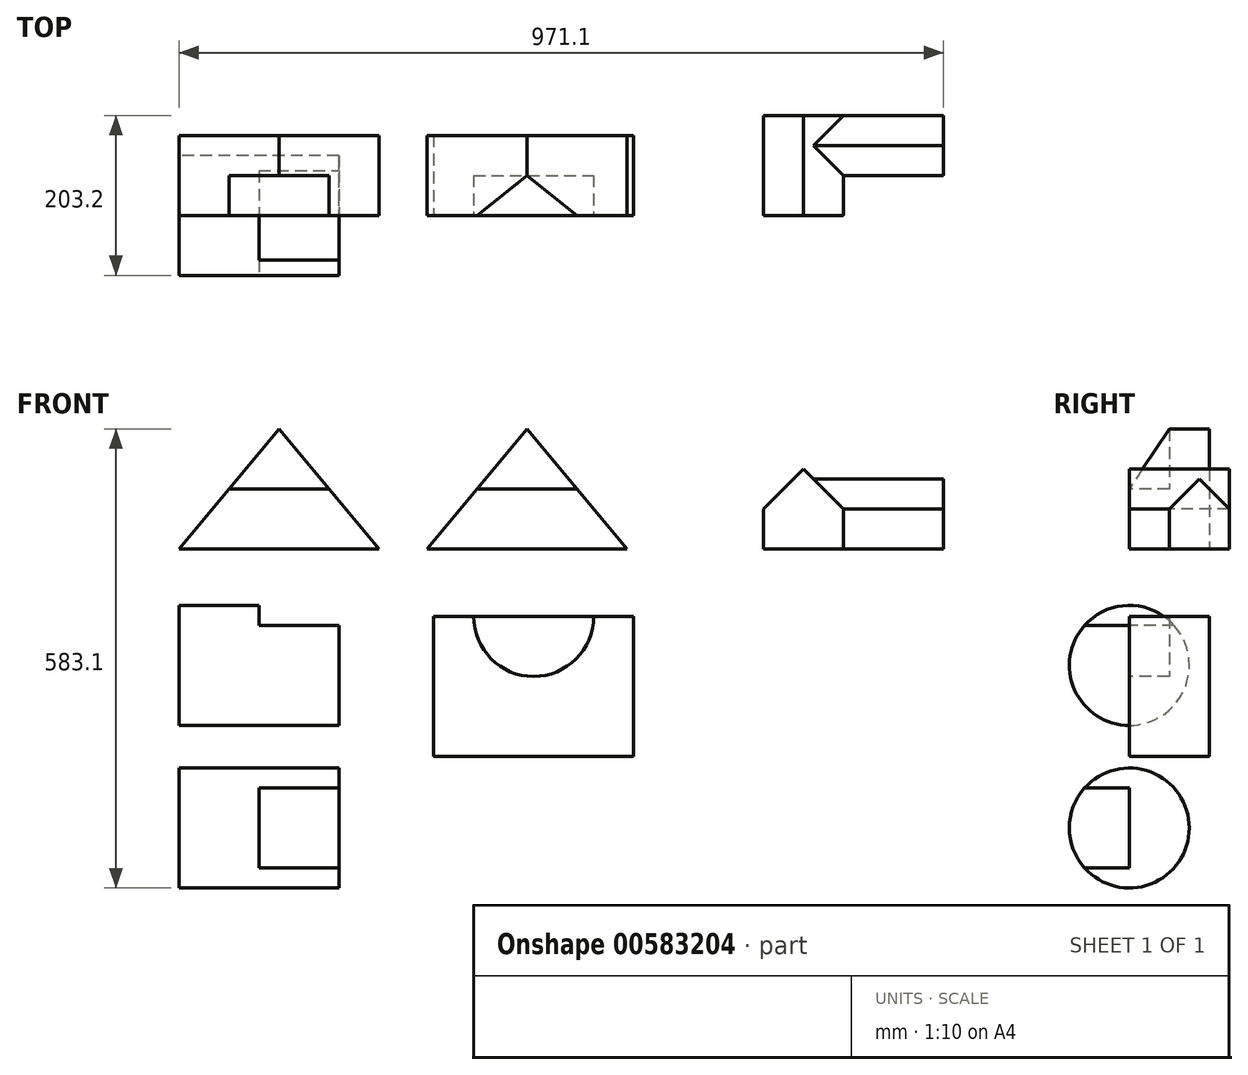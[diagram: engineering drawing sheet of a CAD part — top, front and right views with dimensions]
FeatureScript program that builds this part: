
annotation { "Feature Type Name" : "Feature", "Feature Type Description" : "" }
export const myFeature = defineFeature(function(context is Context, id is Id, definition is map)
    precondition{}
    {
        {
            var Q0;
            Q0=qCreatedBy(makeId("Front.planeOp"),FACE);
            var sketch = newSketch(context, id + "F0", { "sketchPlane" : qUnion([Q0])});
            skLineSegment(sketch, "E0", {"start": v(0, 0) * mm, "end": v(254, 0) * mm});
            skLineSegment(sketch, "E1", {"start": v(127, 152.4) * mm, "end": v(0, 0) * mm});
            skLineSegment(sketch, "E2", {"start": v(127, 152.4) * mm, "end": v(254, 0) * mm});
            skSolve(sketch);
        }
        {
            var Q0;
            Q0=makeQuery(id+"F0.imprint","IMPRINT",FACE,{"disambiguationData":[TD([[makeQuery(id+"F0.imprint","IMPRINT",EDGE,{"derivedFrom":sQuery(id+"F0.wireOp",EDGE,"E0")}),1.0]])]});
            extrude(context, id + "F1", {"entities" : qUnion([Q0]), "oppositeDirection" : true, "depth" : 101.6 * mm, "offsetDistance" : 25.4 * mm});
        }
        {
            var Q0;
            Q0=makeQuery(id+"F1.opExtrude","CAP_FACE",FACE,{"disambiguationData":[OSD([sQuery(id+"F0.wireOp",EDGE,"E0"),sQuery(id+"F0.wireOp",EDGE,"E1"),sQuery(id+"F0.wireOp",EDGE,"E2")])],"isStart":true});
            var sketch = newSketch(context, id + "F2", { "sketchPlane" : qUnion([Q0])});
            skLineSegment(sketch, "E3", {"start": v(127, 76.2) * mm, "end": v(63.5, 76.2) * mm});
            skLineSegment(sketch, "E4", {"start": v(127, 76.2) * mm, "end": v(190.5, 76.2) * mm});
            skLineSegment(sketch, "E5", {"start": v(63.5, 76.2) * mm, "end": v(127, 152.4) * mm});
            skLineSegment(sketch, "E6", {"start": v(127, 152.4) * mm, "end": v(190.5, 76.2) * mm});
            skSolve(sketch);
        }
        {
            var Q0;
            Q0 = qSketchRegion(id + "F2", true);
            extrude(context, id + "F3", {"entities" : qUnion([Q0]), "operationType" : NewBodyOperationType.REMOVE, "oppositeDirection" : true, "depth" : 50.8 * mm, "offsetDistance" : 25.4 * mm});
        }
        {
            var Q0;
            Q0=qCreatedBy(makeId("Front.planeOp"),FACE);
            var sketch = newSketch(context, id + "F4", { "sketchPlane" : qUnion([Q0])});
            skLineSegment(sketch, "E7", {"start": v(315.2, 0) * mm, "end": v(569.2, 0) * mm});
            skLineSegment(sketch, "E8", {"start": v(442.2, 152.4) * mm, "end": v(315.2, 0) * mm});
            skLineSegment(sketch, "E9", {"start": v(442.2, 152.4) * mm, "end": v(569.2, 0) * mm});
            skSolve(sketch);
        }
        {
            var Q0;
            Q0=makeQuery(id+"F4.imprint","IMPRINT",FACE,{"disambiguationData":[TD([[makeQuery(id+"F4.imprint","IMPRINT",EDGE,{"derivedFrom":sQuery(id+"F4.wireOp",EDGE,"E7")}),1.0]])]});
            extrude(context, id + "F5", {"entities" : qUnion([Q0]), "oppositeDirection" : true, "depth" : 101.6 * mm, "offsetDistance" : 25.4 * mm});
        }
        {
            var Q0;
            Q0=makeQuery(id+"F5.opExtrude","CAP_EDGE",EDGE,{"disambiguationData":[OSD([sQuery(id+"F4.wireOp",EDGE,"E7")])],"isStart":true});
            cPoint(context, id + "F6", {"entities" : qUnion([Q0]), "parameter" : 0.5});
        }
        {
            var Q0;
            Q0=makeQuery(id+"F5.opExtrude","CAP_VERTEX",VERTEX,{"disambiguationData":[OSD([sQuery(id+"F4.wireOp",EDGE,"E8"),sQuery(id+"F4.wireOp",EDGE,"E9")])],"isStart":true});
            var Q1;
            Q1=makeQuery(id+"F5.opExtrude","CAP_VERTEX",VERTEX,{"disambiguationData":[OSD([sQuery(id+"F4.wireOp",EDGE,"E8"),sQuery(id+"F4.wireOp",EDGE,"E9")])],"isStart":false});
            var Q2;
            Q2 = qCreatedBy(id + "F6" ,VERTEX);
            cPlane(context, id + "F7", {"entities" : qUnion([Q0, Q1, Q2]), "cplaneType" : CPlaneType.THREE_POINT, "offset" : 127 * mm, "oppositeDirection" : true, "width" : 152.4 * mm, "height" : 152.4 * mm});
        }
        {
            var Q0;
            Q0=qCreatedBy(id+"F7.planeOp",FACE);
            var sketch = newSketch(context, id + "F8", { "sketchPlane" : qUnion([Q0])});
            skLineSegment(sketch, "E10", {"start": v(0, 152.4) * mm, "end": v(50.8, 152.4) * mm});
            skLineSegment(sketch, "E11", {"start": v(0, 152.4) * mm, "end": v(0, 76.2) * mm});
            skLineSegment(sketch, "E12", {"start": v(0, 76.2) * mm, "end": v(50.8, 152.4) * mm});
            skSolve(sketch);
        }
        {
            var Q0;
            Q0 = qSketchRegion(id + "F8", true);
            extrude(context, id + "F9", {"entities" : qUnion([Q0]), "operationType" : NewBodyOperationType.REMOVE, "endBound" : BoundingType.SYMMETRIC, "oppositeDirection" : true, "depth" : 141.22 * mm, "offsetDistance" : 25.4 * mm});
        }
        {
            var Q0;
            Q0=qCreatedBy(makeId("Front.planeOp"),FACE);
            var sketch = newSketch(context, id + "F10", { "sketchPlane" : qUnion([Q0])});
            skLineSegment(sketch, "E13.bottom", {"start": v(742.5, 0) * mm, "end": v(971.1, 0) * mm});
            skLineSegment(sketch, "E13.top", {"start": v(742.5, 101.6) * mm, "end": v(971.1, 101.6) * mm});
            skLineSegment(sketch, "E13.left", {"start": v(742.5, 0) * mm, "end": v(742.5, 101.6) * mm});
            skLineSegment(sketch, "E13.right", {"start": v(971.1, 0) * mm, "end": v(971.1, 101.6) * mm});
            skSolve(sketch);
        }
        {
            var Q0;
            Q0=makeQuery(id+"F10.imprint","IMPRINT",FACE,{"disambiguationData":[TD([[makeQuery(id+"F10.imprint","IMPRINT",EDGE,{"derivedFrom":sQuery(id+"F10.wireOp",EDGE,"E13.bottom")}),1.0]])]});
            extrude(context, id + "F11", {"entities" : qUnion([Q0]), "oppositeDirection" : true, "depth" : 127 * mm, "offsetDistance" : 25.4 * mm});
        }
        {
            var Q0;
            Q0=makeQuery(id+"F11.opExtrude","CAP_FACE",FACE,{"disambiguationData":[OSD([sQuery(id+"F10.wireOp",EDGE,"E13.bottom"),sQuery(id+"F10.wireOp",EDGE,"E13.top"),sQuery(id+"F10.wireOp",EDGE,"E13.left"),sQuery(id+"F10.wireOp",EDGE,"E13.right")])],"isStart":true});
            var sketch = newSketch(context, id + "F12", { "sketchPlane" : qUnion([Q0])});
            skLineSegment(sketch, "E14", {"start": v(742.5, 101.6) * mm, "end": v(793.3, 101.6) * mm});
            skLineSegment(sketch, "E15", {"start": v(742.5, 101.6) * mm, "end": v(742.5, 50.8) * mm});
            skLineSegment(sketch, "E16", {"start": v(793.3, 101.6) * mm, "end": v(742.5, 50.8) * mm});
            skLineSegment(sketch, "E17", {"start": v(793.3, 101.6) * mm, "end": v(844.1, 101.6) * mm});
            skLineSegment(sketch, "E18", {"start": v(844.1, 101.6) * mm, "end": v(844.1, 50.8) * mm});
            skLineSegment(sketch, "E19", {"start": v(844.1, 50.8) * mm, "end": v(793.3, 101.6) * mm});
            skSolve(sketch);
        }
        {
            var Q0;
            Q0 = qSketchRegion(id + "F12", true);
            extrude(context, id + "F13", {"entities" : qUnion([Q0]), "operationType" : NewBodyOperationType.REMOVE, "oppositeDirection" : true, "depth" : 139.7 * mm, "offsetDistance" : 25.4 * mm});
        }
        {
            var Q0;
            Q0=makeQuery(id+"F11.opExtrude","CAP_FACE",FACE,{"disambiguationData":[OSD([sQuery(id+"F10.wireOp",EDGE,"E13.bottom"),sQuery(id+"F10.wireOp",EDGE,"E13.top"),sQuery(id+"F10.wireOp",EDGE,"E13.left"),sQuery(id+"F10.wireOp",EDGE,"E13.right")])],"isStart":true});
            var sketch = newSketch(context, id + "F14", { "sketchPlane" : qUnion([Q0])});
            skPoint(sketch, "E20.endSnap0", {"position": v(971.1, 50.8) * mm});
            skLineSegment(sketch, "E21", {"start": v(844.1, 50.8) * mm, "end": v(844.1, 0) * mm});
            skLineSegment(sketch, "E22.bottom", {"start": v(844.1, 0) * mm, "end": v(971.1, 0) * mm});
            skLineSegment(sketch, "E22.left", {"start": v(844.1, 0) * mm, "end": v(844.1, 50.8) * mm});
            skLineSegment(sketch, "E22.right", {"start": v(971.1, 0) * mm, "end": v(971.1, 50.8) * mm});
            skLineSegment(sketch, "E23", {"start": v(844.1, 50.8) * mm, "end": v(844.1, 101.6) * mm});
            skLineSegment(sketch, "E24", {"start": v(844.1, 101.6) * mm, "end": v(971.1, 101.6) * mm});
            skLineSegment(sketch, "E25", {"start": v(971.1, 101.6) * mm, "end": v(971.1, 50.8) * mm});
            skSolve(sketch);
        }
        {
            var Q0;
            Q0=makeQuery(id+"F11.opExtrude","SWEPT_FACE",FACE,{"disambiguationData":[OSD([sQuery(id+"F10.wireOp",EDGE,"E13.right")])]});
            var sketch = newSketch(context, id + "F15", { "sketchPlane" : qUnion([Q0])});
            skLineSegment(sketch, "E26", {"start": v(50.8, 50.8) * mm, "end": v(88.9, 88.9) * mm});
            skLineSegment(sketch, "E27", {"start": v(88.9, 88.9) * mm, "end": v(127, 50.8) * mm});
            skLineSegment(sketch, "E28", {"start": v(127, 50.8) * mm, "end": v(127, 0) * mm});
            skLineSegment(sketch, "E29", {"start": v(127, 0) * mm, "end": v(50.8, 0) * mm});
            skLineSegment(sketch, "E30", {"start": v(50.8, 0) * mm, "end": v(50.8, 50.8) * mm});
            skSolve(sketch);
        }
        {
            var Q0;
            Q0=makeQuery(id+"F15.imprint","IMPRINT",FACE,{"disambiguationData":[TD([[makeQuery(id+"F15.imprint","IMPRINT",EDGE,{"derivedFrom":sQuery(id+"F15.wireOp",EDGE,"E26")}),-1.0]])]});
            var sketch = newSketch(context, id + "F16", { "sketchPlane" : qUnion([Q0])});
            skLineSegment(sketch, "E31", {"start": v(50.8, 50.8) * mm, "end": v(50.8, 101.6) * mm});
            skLineSegment(sketch, "E32", {"start": v(50.8, 101.6) * mm, "end": v(127, 101.6) * mm});
            skLineSegment(sketch, "E33", {"start": v(127, 101.6) * mm, "end": v(127, 50.8) * mm});
            skLineSegment(sketch, "E34", {"start": v(50.8, 50.8) * mm, "end": v(88.9, 88.9) * mm});
            skLineSegment(sketch, "E35", {"start": v(88.9, 88.9) * mm, "end": v(127, 50.8) * mm});
            skSolve(sketch);
        }
        {
            var Q0;
            Q0 = qSketchRegion(id + "F14", true);
            extrude(context, id + "F17", {"entities" : qUnion([Q0]), "operationType" : NewBodyOperationType.REMOVE, "oppositeDirection" : true, "depth" : 50.8 * mm, "offsetDistance" : 25.4 * mm});
        }
        {
            var Q0;
            Q0=makeQuery(id+"F15.imprint","IMPRINT",FACE,{"disambiguationData":[TD([[makeQuery(id+"F15.imprint","IMPRINT",EDGE,{"derivedFrom":sQuery(id+"F15.wireOp",EDGE,"E26")}),1.0]])]});
            extrude(context, id + "F18", {"entities" : qUnion([Q0]), "operationType" : NewBodyOperationType.REMOVE, "oppositeDirection" : true, "depth" : 127 * mm, "offsetDistance" : 25.4 * mm});
        }
        {
            var Q0;
            Q0=makeQuery(id+"F16.imprint","IMPRINT",FACE,{"disambiguationData":[TD([[makeQuery(id+"F16.imprint","IMPRINT",EDGE,{"derivedFrom":sQuery(id+"F16.wireOp",EDGE,"E34")}),-1.0]])]});
            extrude(context, id + "F19", {"entities" : qUnion([Q0]), "operationType" : NewBodyOperationType.ADD, "oppositeDirection" : true, "depth" : 177.8 * mm, "offsetDistance" : 25.4 * mm});
        }
        {
            var Q0;
            Q0=qCreatedBy(makeId("Right.planeOp"),FACE);
            var sketch = newSketch(context, id + "F20", { "sketchPlane" : qUnion([Q0])});
            skCircle(sketch, "E36", {"center": v(0, -147.9) * mm, "radius": 76.2 * mm});
            skSolve(sketch);
        }
        {
            var Q0;
            Q0=makeQuery(id+"F20.imprint","IMPRINT",FACE,{"disambiguationData":[TD([[makeQuery(id+"F20.imprint","IMPRINT",EDGE,{"derivedFrom":sQuery(id+"F20.wireOp",EDGE,"E36")}),1.0]])]});
            extrude(context, id + "F21", {"entities" : qUnion([Q0]), "depth" : 203.2 * mm, "offsetDistance" : 25.4 * mm});
        }
        {
            var Q0;
            Q0=makeQuery(id+"F21.opExtrude","CAP_FACE",FACE,{"disambiguationData":[OSD([sQuery(id+"F20.wireOp",EDGE,"E36")])],"isStart":false});
            var sketch = newSketch(context, id + "F22", { "sketchPlane" : qUnion([Q0])});
            skLineSegment(sketch, "E37", {"start": v(0, -97.1) * mm, "end": v(-56.8, -97.1) * mm});
            skLineSegment(sketch, "E38", {"start": v(0, -97.1) * mm, "end": v(56.8, -97.1) * mm});
            skSolve(sketch);
        }
        {
            var Q0;
            {var subQ0=sQuery(id+"F22.wireOp",EDGE,"E37");Q0=makeQuery(id+"F22.imprint","IMPRINT",FACE,{"disambiguationData":[TD([[makeQuery(id+"F22.imprint","IMPRINT",EDGE,{"derivedFrom":subQ0}),-1.0]])]});}
            extrude(context, id + "F23", {"entities" : qUnion([Q0]), "operationType" : NewBodyOperationType.REMOVE, "oppositeDirection" : true, "depth" : 101.6 * mm, "offsetDistance" : 25.4 * mm});
        }
        {
            var Q0;
            Q0=qCreatedBy(makeId("Right.planeOp"),FACE);
            var sketch = newSketch(context, id + "F24", { "sketchPlane" : qUnion([Q0])});
            skCircle(sketch, "E39", {"center": v(0, -354.5) * mm, "radius": 76.2 * mm});
            skSolve(sketch);
        }
        {
            var Q0;
            Q0=makeQuery(id+"F24.imprint","IMPRINT",FACE,{"disambiguationData":[TD([[makeQuery(id+"F24.imprint","IMPRINT",EDGE,{"derivedFrom":sQuery(id+"F24.wireOp",EDGE,"E39")}),1.0]])]});
            extrude(context, id + "F25", {"entities" : qUnion([Q0]), "depth" : 203.2 * mm, "offsetDistance" : 25.4 * mm});
        }
        {
            var Q0;
            Q0=makeQuery(id+"F25.opExtrude","CAP_FACE",FACE,{"disambiguationData":[OSD([sQuery(id+"F24.wireOp",EDGE,"E39")])],"isStart":false});
            var sketch = newSketch(context, id + "F26", { "sketchPlane" : qUnion([Q0])});
            skLineSegment(sketch, "E40", {"start": v(0, -354.5) * mm, "end": v(0, -303.7) * mm});
            skLineSegment(sketch, "E41", {"start": v(0, -354.5) * mm, "end": v(0, -405.3) * mm});
            skLineSegment(sketch, "E42", {"start": v(0, -303.7) * mm, "end": v(-56.8, -303.7) * mm});
            skLineSegment(sketch, "E43", {"start": v(0, -405.3) * mm, "end": v(-56.8, -405.3) * mm});
            skSolve(sketch);
        }
        {
            var Q0;
            Q0=makeQuery(id+"F26.imprint","IMPRINT",FACE,{"disambiguationData":[TD([[makeQuery(id+"F26.imprint","IMPRINT",EDGE,{"derivedFrom":sQuery(id+"F26.wireOp",EDGE,"E40")}),1.0]])]});
            extrude(context, id + "F27", {"entities" : qUnion([Q0]), "operationType" : NewBodyOperationType.REMOVE, "oppositeDirection" : true, "depth" : 101.6 * mm, "offsetDistance" : 25.4 * mm});
        }
        {
            var Q0;
            Q0=qCreatedBy(makeId("Front.planeOp"),FACE);
            var sketch = newSketch(context, id + "F28", { "sketchPlane" : qUnion([Q0])});
            skLineSegment(sketch, "E44.bottom", {"start": v(323.57, -263.53) * mm, "end": v(577.57, -263.53) * mm});
            skLineSegment(sketch, "E44.top", {"start": v(323.57, -85.73) * mm, "end": v(577.57, -85.73) * mm});
            skLineSegment(sketch, "E44.left", {"start": v(323.57, -263.53) * mm, "end": v(323.57, -85.73) * mm});
            skLineSegment(sketch, "E44.right", {"start": v(577.57, -263.53) * mm, "end": v(577.57, -85.73) * mm});
            skSolve(sketch);
        }
        {
            var Q0;
            Q0=makeQuery(id+"F28.imprint","IMPRINT",FACE,{"disambiguationData":[TD([[makeQuery(id+"F28.imprint","IMPRINT",EDGE,{"derivedFrom":sQuery(id+"F28.wireOp",EDGE,"E44.bottom")}),1.0]])]});
            extrude(context, id + "F29", {"entities" : qUnion([Q0]), "oppositeDirection" : true, "depth" : 101.6 * mm, "offsetDistance" : 25.4 * mm});
        }
        {
            var Q0;
            Q0=makeQuery(id+"F29.opExtrude","CAP_FACE",FACE,{"disambiguationData":[OSD([sQuery(id+"F28.wireOp",EDGE,"E44.bottom"),sQuery(id+"F28.wireOp",EDGE,"E44.top"),sQuery(id+"F28.wireOp",EDGE,"E44.left"),sQuery(id+"F28.wireOp",EDGE,"E44.right")])],"isStart":true});
            var sketch = newSketch(context, id + "F30", { "sketchPlane" : qUnion([Q0])});
            skCircle(sketch, "E45", {"center": v(450.57, -85.73) * mm, "radius": 76.2 * mm});
            skSolve(sketch);
        }
        {
            var Q0;
            {var subQ0=sQuery(id+"F30.wireOp",EDGE,"E45");var subQ1=makeQuery(id+"F29.opExtrude","CAP_EDGE",EDGE,{"disambiguationData":[OSD([sQuery(id+"F28.wireOp",EDGE,"E44.top")])],"isStart":true});var subQ2=makeQuery(id+"F30.imprint","INTERSECT",VERTEX,{"disambiguationData":[OD(0.0)],"derivedFrom":[subQ1,subQ0]});Q0=makeQuery(id+"F30.imprint","IMPRINT",FACE,{"disambiguationData":[TD([[makeQuery(id+"F30.imprint","IMPRINT",EDGE,{"disambiguationData":[TD([[subQ2,-1.0]])],"derivedFrom":subQ0}),1.0]])]});}
            extrude(context, id + "F31", {"entities" : qUnion([Q0]), "operationType" : NewBodyOperationType.REMOVE, "oppositeDirection" : true, "depth" : 50.8 * mm, "offsetDistance" : 25.4 * mm});
        }
    });
